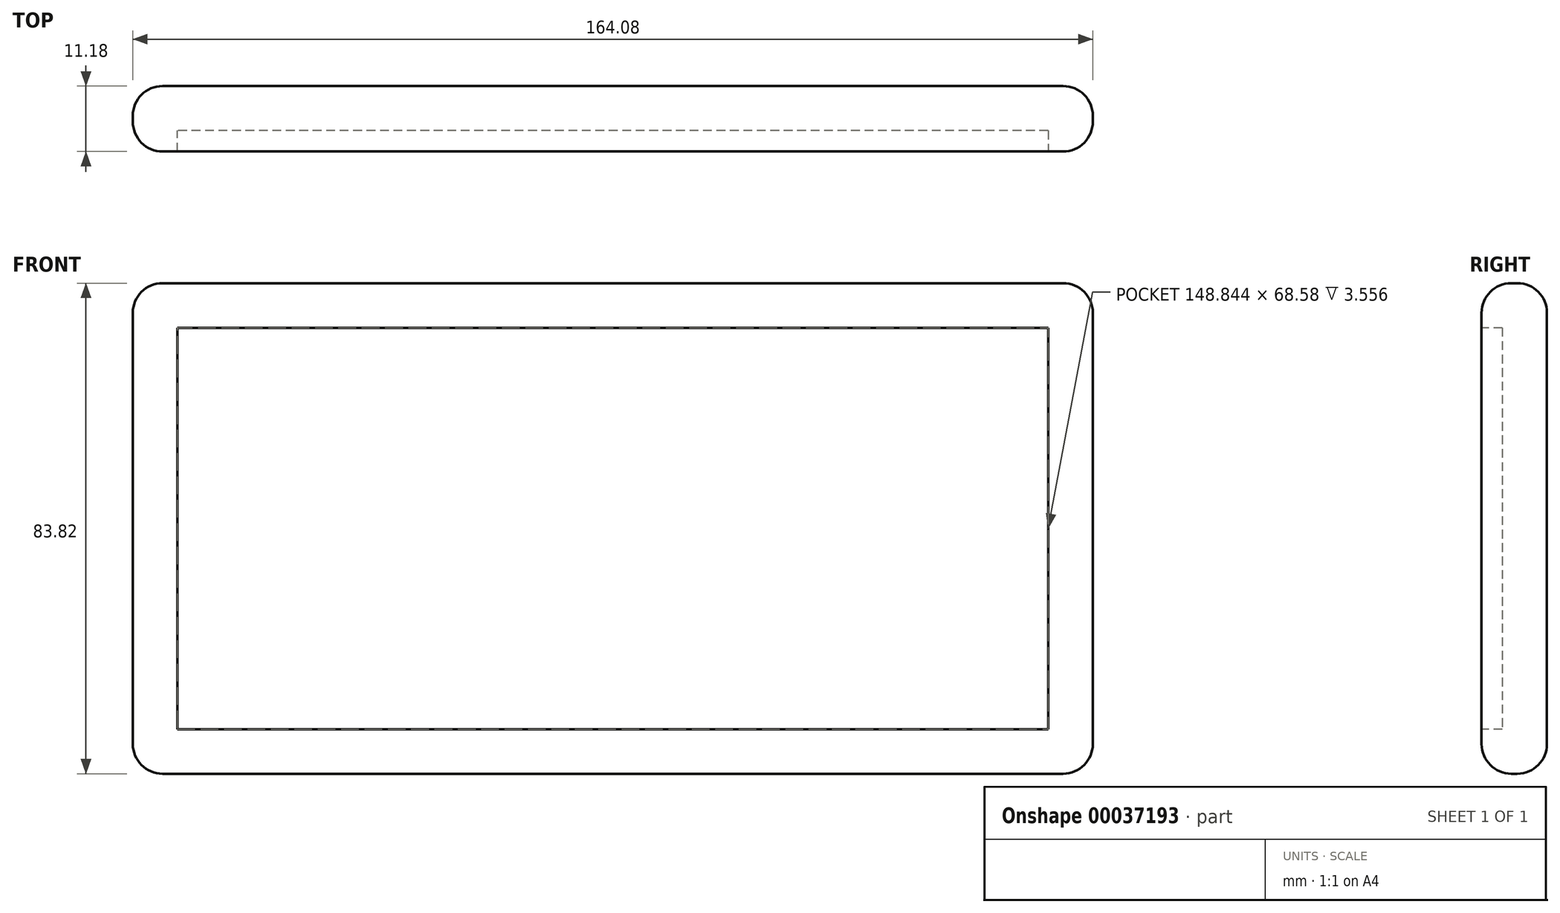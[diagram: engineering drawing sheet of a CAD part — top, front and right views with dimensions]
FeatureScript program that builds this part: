
annotation { "Feature Type Name" : "Feature", "Feature Type Description" : "" }
export const myFeature = defineFeature(function(context is Context, id is Id, definition is map)
    precondition{}
    {
        {
            var Q0;
            Q0=qCreatedBy(makeId("Front.planeOp"),FACE);
            var sketch = newSketch(context, id + "F0", { "sketchPlane" : qUnion([Q0])});
            skLineSegment(sketch, "E0.bottom", {"start": v(0, 0) * mm, "end": v(-164.08, 0) * mm});
            skLineSegment(sketch, "E0.top", {"start": v(0, 83.82) * mm, "end": v(-164.08, 83.82) * mm});
            skLineSegment(sketch, "E0.left", {"start": v(0, 0) * mm, "end": v(0, 83.82) * mm});
            skLineSegment(sketch, "E0.right", {"start": v(-164.08, 0) * mm, "end": v(-164.08, 83.82) * mm});
            skSolve(sketch);
        }
        {
            var Q0;
            Q0=makeQuery(id+"F0.imprint","IMPRINT",FACE,{"disambiguationData":[TD([[makeQuery(id+"F0.imprint","IMPRINT",EDGE,{"derivedFrom":sQuery(id+"F0.wireOp",EDGE,"E0.bottom")}),-1.0]])]});
            extrude(context, id + "F1", {"entities" : qUnion([Q0]), "depth" : 11.18 * mm});
        }
        {
            var Q0;
            Q0=makeQuery(id+"F1.opExtrude","CAP_EDGE",EDGE,{"disambiguationData":[OSD([sQuery(id+"F0.wireOp",EDGE,"E0.top")])],"isStart":false});
            fillet(context, id + "F2", {"entities" : qUnion([Q0]), "radius" : 5.08 * mm, "tangentPropagation" : true, "allowEdgeOverflow" : false});
        }
        {
            var Q0;
            Q0=makeQuery(id+"F1.opExtrude","CAP_EDGE",EDGE,{"disambiguationData":[OSD([sQuery(id+"F0.wireOp",EDGE,"E0.top")])],"isStart":true});
            fillet(context, id + "F3", {"entities" : qUnion([Q0]), "radius" : 5.08 * mm, "tangentPropagation" : true, "allowEdgeOverflow" : false});
        }
        {
            var Q0;
            Q0=makeQuery(id+"F1.opExtrude","CAP_EDGE",EDGE,{"disambiguationData":[OSD([sQuery(id+"F0.wireOp",EDGE,"E0.bottom")])],"isStart":true});
            fillet(context, id + "F4", {"entities" : qUnion([Q0]), "radius" : 5.08 * mm, "tangentPropagation" : true, "allowEdgeOverflow" : false});
        }
        {
            var Q0;
            Q0=makeQuery(id+"F1.opExtrude","CAP_EDGE",EDGE,{"disambiguationData":[OSD([sQuery(id+"F0.wireOp",EDGE,"E0.bottom")])],"isStart":false});
            fillet(context, id + "F5", {"entities" : qUnion([Q0]), "radius" : 5.08 * mm, "tangentPropagation" : true, "allowEdgeOverflow" : false});
        }
        {
            var Q0;
            Q0=makeQuery(id+"F1.opExtrude","SWEPT_FACE",FACE,{"disambiguationData":[OSD([sQuery(id+"F0.wireOp",EDGE,"E0.left")])]});
            fillet(context, id + "F6", {"entities" : qUnion([Q0]), "radius" : 5.08 * mm, "tangentPropagation" : true, "allowEdgeOverflow" : false});
        }
        {
            var Q0;
            Q0=makeQuery(id+"F1.opExtrude","SWEPT_FACE",FACE,{"disambiguationData":[OSD([sQuery(id+"F0.wireOp",EDGE,"E0.right")])]});
            fillet(context, id + "F7", {"entities" : qUnion([Q0]), "radius" : 5.08 * mm, "tangentPropagation" : true, "allowEdgeOverflow" : false});
        }
        {
            var Q0;
            Q0=makeQuery(id+"F1.opExtrude","CAP_FACE",FACE,{"disambiguationData":[OSD([sQuery(id+"F0.wireOp",EDGE,"E0.bottom"),sQuery(id+"F0.wireOp",EDGE,"E0.top"),sQuery(id+"F0.wireOp",EDGE,"E0.left"),sQuery(id+"F0.wireOp",EDGE,"E0.right")])],"isStart":false});
            shell(context, id + "F8", {"entities" : qUnion([Q0]), "thickness" : 7.62 * mm});
        }
    });
